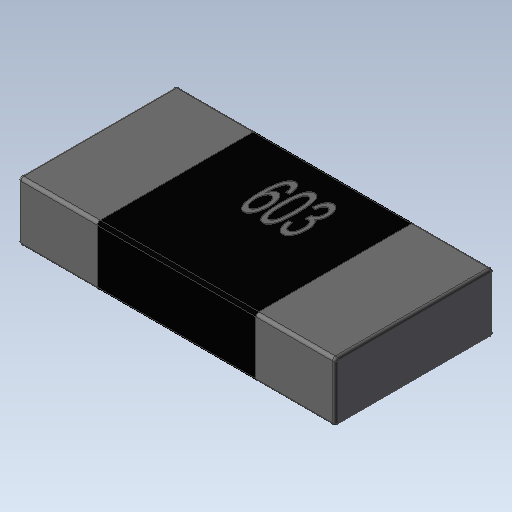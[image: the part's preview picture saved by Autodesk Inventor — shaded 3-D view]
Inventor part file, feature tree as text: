
AUTODESK INVENTOR PART (.ipt)
format: ipt  version: 2020 (Build 240168000, 168)  size: 249,344 bytes
history: native  units: in
note: dims shown in document units (in); Inventor stores cm internally (conversion verified against a paired STEP export)
features: extrude x1
ambient origin geometry x8: Origin, YZ Plane, XZ Plane, XY Plane, X Axis, Y Axis, Z Axis, Center Point
bodies: Solid1 (feature_tree)
feature tree (1):
  extrude  "Extrude2"  [1 undecoded]
note: 1 required parameter value undecoded (feature->parameter linkage not recoverable at this tier; creation-order binding heuristic only, values carry confidence <= 0.55)
